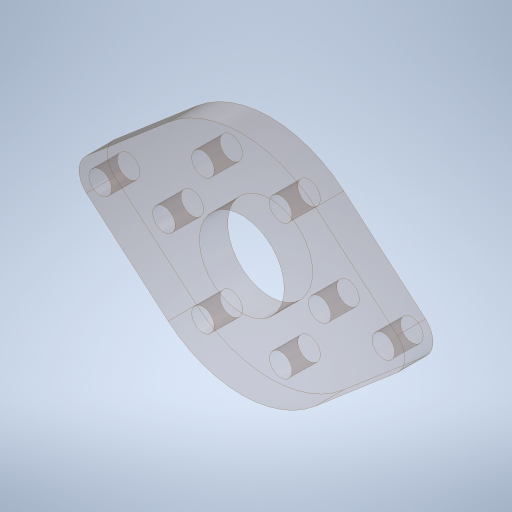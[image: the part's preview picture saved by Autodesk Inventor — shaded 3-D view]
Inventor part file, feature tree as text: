
AUTODESK INVENTOR PART (.ipt)
format: ipt  version: 2023.4 (Build 274418000, 418)  size: 304,640 bytes
history: native  units: in
note: dims shown in document units (in); Inventor stores cm internally (conversion verified against a paired STEP export)
features: sketch x1, extrude x1, hole x1
ambient origin geometry x8: Origin, YZ Plane, XZ Plane, XY Plane, X Axis, Y Axis, Z Axis, Center Point
bodies: Solid1 (feature_tree)
feature tree (3):
  sketch  "Sketch1"  dims[d0=0.75in d1=2.0in d2=0.375in d3=1.375in d4=2.3622in d6=360.0deg d8=0.25in d9=0.0in d10=0.201in d11=0.75in d12=0.385in d13=0.25in d14=0.5635in d15=1.0in d16=0.8108in d17=2.5in]
  extrude  "Extrusion1"  Depth=2.0in
  hole  "Hole1"  [1 undecoded]
note: 1 required parameter value undecoded (feature->parameter linkage not recoverable at this tier; creation-order binding heuristic only, values carry confidence <= 0.55)
